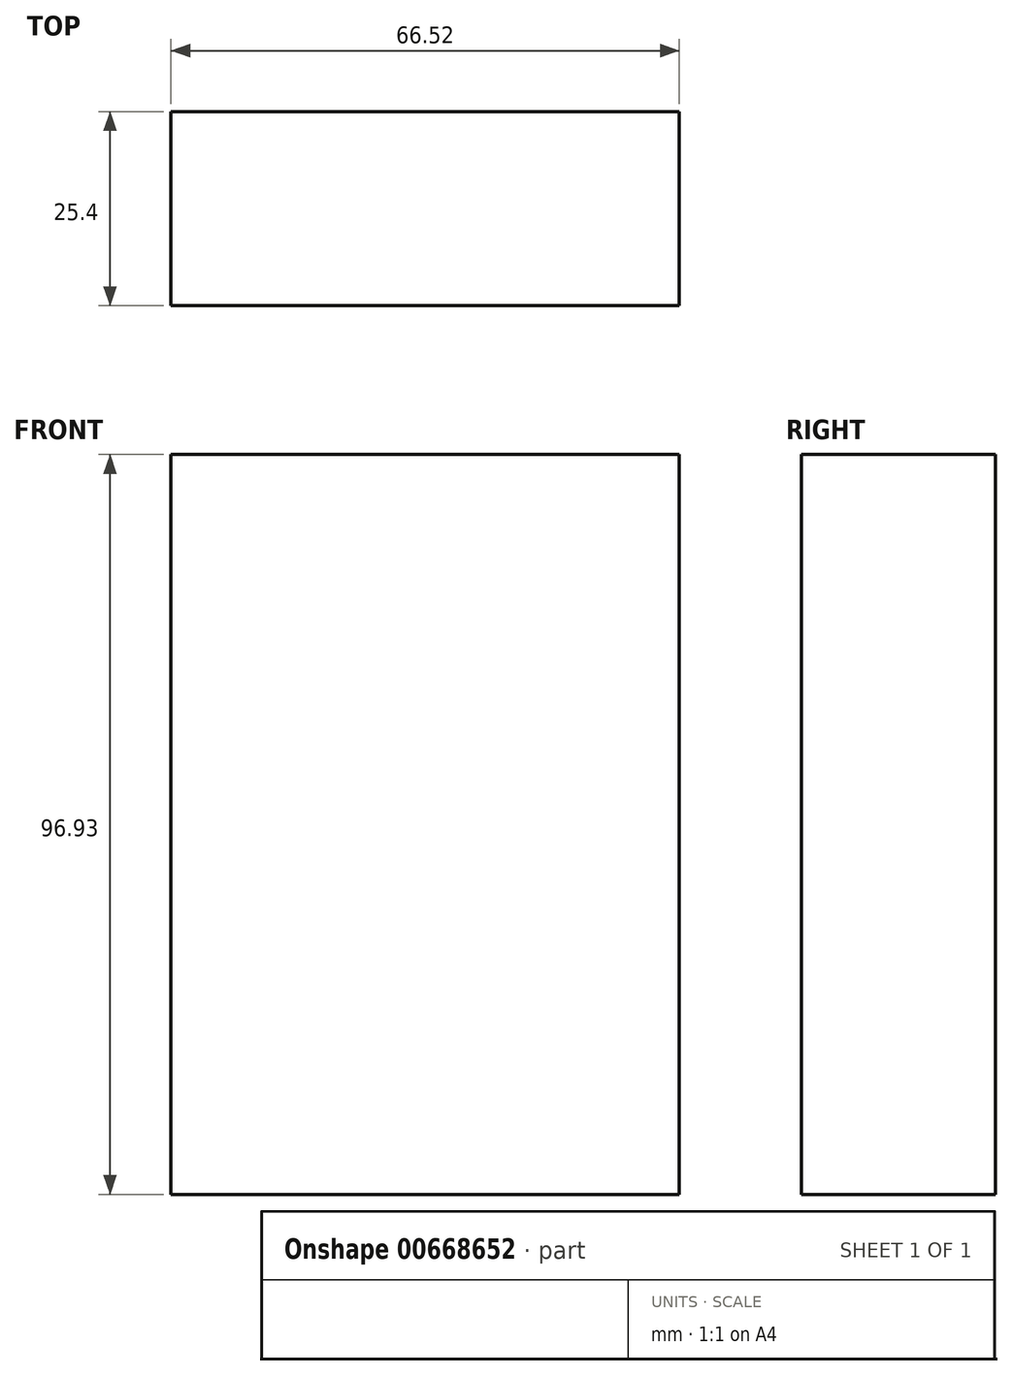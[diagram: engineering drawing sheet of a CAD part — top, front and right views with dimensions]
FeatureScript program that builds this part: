
annotation { "Feature Type Name" : "Feature", "Feature Type Description" : "" }
export const myFeature = defineFeature(function(context is Context, id is Id, definition is map)
    precondition{}
    {
        {
            var Q0;
            Q0=qCreatedBy(makeId("Front.planeOp"),FACE);
            var sketch = newSketch(context, id + "F0", { "sketchPlane" : qUnion([Q0])});
            skLineSegment(sketch, "E0.bottom", {"start": v(-139.7, 114.3) * mm, "end": v(139.7, 114.3) * mm});
            skLineSegment(sketch, "E0.top", {"start": v(-139.7, -114.3) * mm, "end": v(139.7, -114.3) * mm});
            skLineSegment(sketch, "E0.left", {"start": v(-139.7, 114.3) * mm, "end": v(-139.7, -114.3) * mm});
            skLineSegment(sketch, "E0.right", {"start": v(139.7, 114.3) * mm, "end": v(139.7, -114.3) * mm});
            skPoint(sketch, "E0.middle", {"position": v(0, 0) * mm});
            skLineSegment(sketch, "E1.bottom", {"start": v(-139.7, 114.3) * mm, "end": v(-71.28, 114.3) * mm});
            skLineSegment(sketch, "E1.top", {"start": v(-139.7, 43.46) * mm, "end": v(-71.28, 43.46) * mm});
            skLineSegment(sketch, "E1.left", {"start": v(-139.7, 114.3) * mm, "end": v(-139.7, 43.46) * mm});
            skLineSegment(sketch, "E1.right", {"start": v(-71.28, 114.3) * mm, "end": v(-71.28, 43.46) * mm});
            skLineSegment(sketch, "E2.bottom", {"start": v(139.7, -17.37) * mm, "end": v(73.18, -17.37) * mm});
            skLineSegment(sketch, "E2.top", {"start": v(139.7, -114.3) * mm, "end": v(73.18, -114.3) * mm});
            skLineSegment(sketch, "E2.left", {"start": v(139.7, -17.37) * mm, "end": v(139.7, -114.3) * mm});
            skLineSegment(sketch, "E2.right", {"start": v(73.18, -17.37) * mm, "end": v(73.18, -114.3) * mm});
            skLineSegment(sketch, "E3.left", {"start": v(139.7, 114.3) * mm, "end": v(139.7, 41.56) * mm});
            skPoint(sketch, "E3.top.end.orphan", {"position": v(73.18, 41.56) * mm});
            skLineSegment(sketch, "E4.bottom", {"start": v(100.26, 114.3) * mm, "end": v(139.7, 114.3) * mm});
            skLineSegment(sketch, "E4.top", {"start": v(100.26, 18.04) * mm, "end": v(139.7, 18.04) * mm});
            skLineSegment(sketch, "E4.left", {"start": v(100.26, 114.3) * mm, "end": v(100.26, 18.04) * mm});
            skLineSegment(sketch, "E4.right", {"start": v(139.7, 114.3) * mm, "end": v(139.7, 18.04) * mm});
            skPoint(sketch, "E5.0.internal.orphan", {"position": v(73.18, -65.83) * mm});
            skArc(sketch, "E6", {"start": v(100.26, 58.6) * mm, "mid": v(45.88, 5.27) * mm, "end": v(73.18, -65.83) * mm});
            skPoint(sketch, "E7.startSnap0", {"position": v(-105.49, 43.46) * mm});
            skPoint(sketch, "E8.orphan", {"position": v(-105.49, 41.56) * mm});
            skArc(sketch, "E9", {"start": v(-105.49, 41.56) * mm, "mid": v(-44.78, -62) * mm, "end": v(73.18, -84.2) * mm});
            skLineSegment(sketch, "E10.bottom", {"start": v(-56.19, 114.3) * mm, "end": v(73.1, 114.3) * mm});
            skLineSegment(sketch, "E10.top", {"start": v(-56.19, 56.44) * mm, "end": v(73.1, 56.44) * mm});
            skLineSegment(sketch, "E10.left", {"start": v(-56.19, 114.3) * mm, "end": v(-56.19, 56.44) * mm});
            skLineSegment(sketch, "E10.right", {"start": v(73.1, 114.3) * mm, "end": v(73.1, 56.44) * mm});
            skArc(sketch, "E11", {"start": v(-13.74, 56.44) * mm, "mid": v(27.98, -16.95) * mm, "end": v(109.76, -37.88) * mm});
            skSolve(sketch);
        }
        {
            var Q0;
            Q0=makeQuery(id+"F0.imprint","IMPRINT",FACE,{"disambiguationData":[TD([[makeQuery(id+"F0.imprint","IMPRINT",EDGE,{"derivedFrom":sQuery(id+"F0.wireOp",EDGE,"E1.bottom")}),-1.0]])]});
            var Q1;
            Q1=makeQuery(id+"F0.imprint","IMPRINT",FACE,{"disambiguationData":[TD([[makeQuery(id+"F0.imprint","IMPRINT",EDGE,{"derivedFrom":sQuery(id+"F0.wireOp",EDGE,"E10.bottom")}),-1.0]])]});
            var Q2;
            {var subQ3=sQuery(id+"F0.wireOp",EDGE,"E4.bottom");Q2=makeQuery(id+"F0.imprint","IMPRINT",FACE,{"disambiguationData":[TD([[makeQuery(id+"F0.imprint","IMPRINT",EDGE,{"derivedFrom":subQ3}),-1.0]])]});}
            var Q3;
            {var subQ1=sQuery(id+"F0.wireOp",EDGE,"E2.bottom");Q3=makeQuery(id+"F0.imprint","IMPRINT",FACE,{"disambiguationData":[TD([[makeQuery(id+"F0.imprint","IMPRINT",EDGE,{"derivedFrom":subQ1}),1.0]])]});}
            extrude(context, id + "F1", {"entities" : qUnion([Q0, Q1, Q2, Q3]), "depth" : 25.4 * mm, "offsetDistance" : 25.4 * mm});
        }
    });
